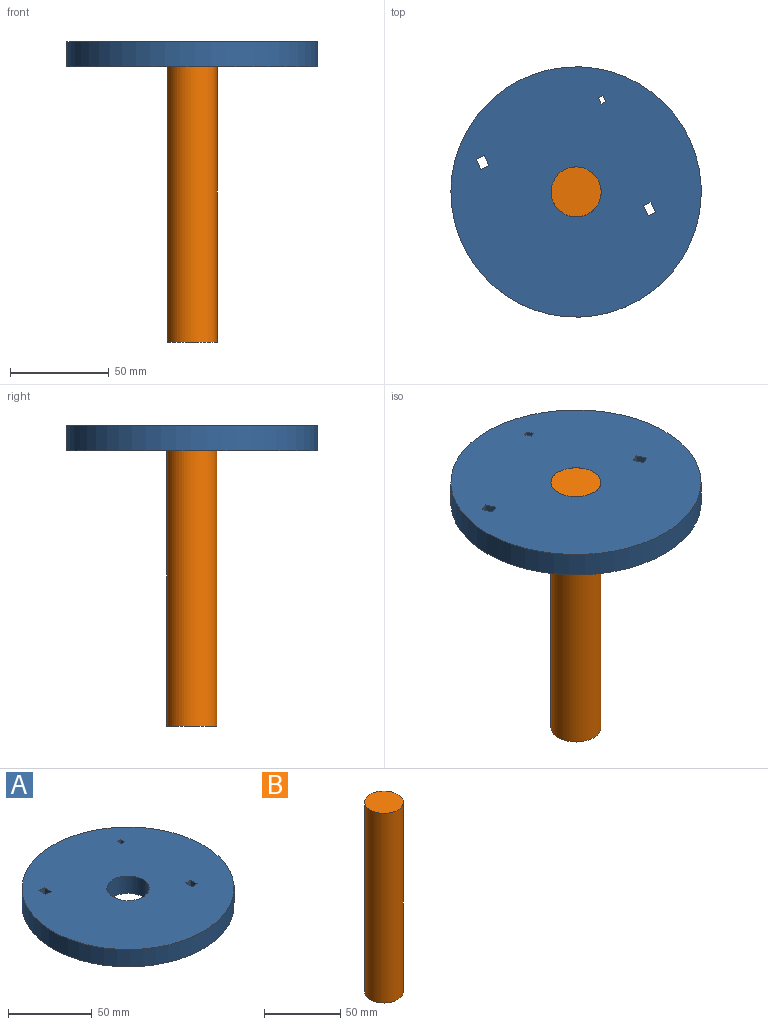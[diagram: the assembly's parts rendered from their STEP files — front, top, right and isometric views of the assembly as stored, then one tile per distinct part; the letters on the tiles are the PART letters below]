
ASSEMBLY  parts=2 mates=1
PART A: 16 faces, bbox 127x127x12.7 mm
  f0: plane 12.7x4.22mm, normal (0,1,0), area 53.6mm2, adj f1,f9,f14,f15
  f1: plane 12.7x5.63mm, normal (1,0,0), area 71.5mm2, adj f0,f2,f14,f15
  f2: plane 12.7x4.22mm, normal (0,-1,0), area 53.6mm2, adj f1,f9,f14,f15
  f3: plane 12.7x2.58mm, normal (0,1,0), area 32.8mm2, adj f4,f10,f14,f15
  f4: plane 12.7x3.52mm, normal (1,0,0), area 44.7mm2, adj f3,f5,f14,f15
  f5: plane 12.7x2.58mm, normal (0,-1,0), area 32.8mm2, adj f4,f10,f14,f15
  f6: plane 12.7x4.46mm, normal (0,1,0), area 56.6mm2, adj f7,f11,f14,f15
  f7: plane 12.7x5.87mm, normal (1,0,0), area 74.5mm2, adj f6,f8,f14,f15
  f8: plane 12.7x4.46mm, normal (0,-1,0), area 56.6mm2, adj f7,f11,f14,f15
  f9: plane 12.7x5.63mm, normal (-1,0,0), area 71.5mm2, adj f0,f2,f14,f15
  f10: plane 12.7x3.52mm, normal (-1,0,0), area 44.7mm2, adj f3,f5,f14,f15
  f11: plane 12.7x5.87mm, normal (-1,0,0), area 74.5mm2, adj f6,f8,f14,f15
  f12: cylinder r=12.7mm len=25.4mm, axis (0,0,-1), area 1013.4mm2, adj f14,f15
  f13: cylinder r=63.5mm len=127mm, axis (0,0,-1), area 5067.1mm2, adj f14,f15
  f14: plane 127x127mm, normal (0,0,1), area 12102mm2, adj f0,f1,f2,f3,f4,f5,f6,f7
  f15: plane 127x127mm, normal (0,0,-1), area 12102mm2, adj f0,f1,f2,f3,f4,f5,f6,f7
PART B: 3 faces, bbox 25.4x25.4x152.4 mm
  f0: cylinder r=12.7mm len=152.4mm, axis (0,0,-1), area 12161mm2, adj f1,f2
  f1: plane 25.4x25.4mm, normal (0,0,1), area 506.7mm2, adj f0
  f2: plane 25.4x25.4mm, normal (0,0,-1), area 506.7mm2, adj f0
PLACE A rot(axis=(0,0,1),24.4deg) t=(-71.58,-71.06,12.82)mm
PLACE B t=(-71.58,-71.06,-57.03)mm fixed
MATE revolute B.f0 <-> A.f12  axis (0,0,1) through (-71.58,-71.06,19.17)mm
